# Revit family: Haworth_Planes_ConferenceTable_RectangularOnePiece
name_source: partatom
category: Furniture Systems
revit_build: Autodesk Revit 2018 (Build: 20170223_1515(x64)
units: mm (PartAtom-declared; Revit-internal decimal feet)

## family parameters
Always vertical = Yes
Cut with Voids When Loaded = No
OmniClass Number = 23.40.70.14.64.21
OmniClass Title = Systems Furniture
Part Type = Normal
Room Calculation Point = No
Round Connector Dimension = Use Diameter
Shared = No
Work Plane-Based = No

## types (4) — shared parameters
Actual Depth = 60"
Actual Height = 29"
Assembly Code = E2020200
Cable Base = Yes
Cable Base 14x14 = Yes
Cable Base Control = Yes
Custom Size = No
Cutout = Yes
Depth = 60"
Edgeband = Yes
Knife Edge = No
Manufacturer = Haworth
Max. Depth = 60"
Max. Height = 29"
Max. Width = 120"
Middle Leg Off_Override = No
Min. Depth = 30"
Min. Height = 29"
Min. Width = 66"
Min/Max Width = 42-120 @ 6 in. increments
Model = TARQ, TARA
Opening Center = Yes
Opening Double = No
Opening Double Wide = No
Opening Left/Right = No
Opening Single = Yes
Opening Single Wide = No
Revision Number = 3
Size = Verify Final Dim. w/ Haworth
Standard Depths = 30, 36, 42, 48, 54, 60 in.
Standard Height = 29 in.
Support Height = 27 13/16"
Sustainability Info = https://www.haworth.com
Table Thickness = 1 3/16"
URL = www.haworth.com
URL - Product = http://www.haworth.com
Warranty = http://www.haworth.com

## per-type parameters (varying)
| type | Actual Width | Description | Interior Leg | Middle Leg | Middle Leg_Interior | Middle Leg_Perimeter | Perimeter Leg | Support Location_Front_Back | Support Location_Side | Width |
| 120w 60d - Interior Leg | 120" | Haworth - Planes Conference Table - Rectangular One Piece - Interior Leg - 120w 60d | Yes | Yes | Yes | No | No | 3" | 3" | 120" |
| 120w 60d - Perimeter Leg | 120" | Haworth - Planes Conference Table - Rectangular One Piece - Perimeter Leg - 120w 60d | No | Yes | No | Yes | Yes | 3/4" | 1 5/8" | 120" |
| 60w 60d - Perimeter Leg | 66" | Haworth - Planes Conference Table - Rectangular One Piece - Perimeter Leg - 60w 60d | No | No | No | No | Yes | 3/4" | 1 5/8" | 60" |
| 60w 60d - Interior Leg | 66" | Haworth - Planes Conference Table - Rectangular One Piece - Interior Leg - 60w 60d | Yes | No | No | No | No | 3" | 3" | 60" |

## geometry (parser evidence)
native form markers: Sweep x8
no freeform markers — native parametric forms only
